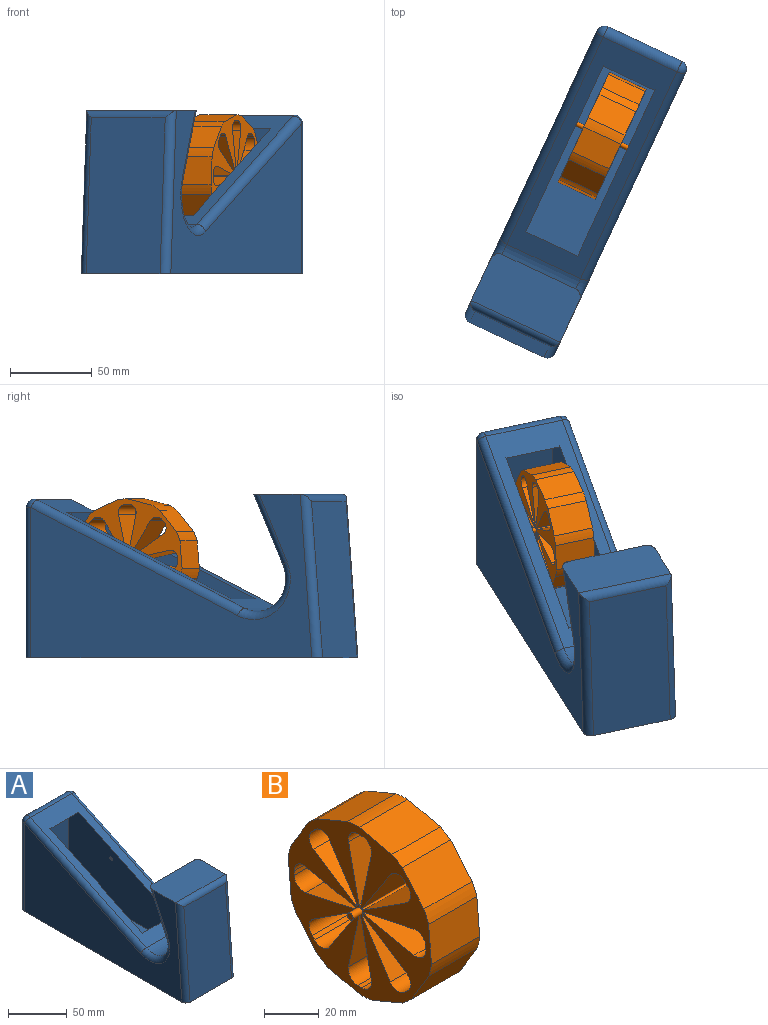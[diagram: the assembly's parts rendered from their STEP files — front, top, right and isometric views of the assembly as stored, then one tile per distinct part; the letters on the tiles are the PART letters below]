
ASSEMBLY  parts=2 mates=1
PART A: 33 faces, bbox 60x200x102.5 mm
  f0: plane 139.81x66.38mm, normal (0,-0.43,0.9), area 3401.7mm2, adj f1,f12,f15,f17,f23,f26,f27,f28
  f1: cylinder r=20mm len=50mm, axis (-1,0,0), area 2441.2mm2, adj f0,f2,f10,f18
  f2: plane 50x43.42mm, normal (0,0.91,-0.41), area 2385.1mm2, adj f1,f3,f9,f19
  f3: plane 60x33.55mm, normal (0,0,1), area 2001.4mm2, adj f2,f7,f8,f9,f19,f20,f21,f22
  f4: plane 95.39x50mm, normal (0,-1,0.08), area 4784.2mm2, adj f5,f20,f21,f22
  f5: plane 200x60mm, normal (0,0,-1), area 11978.5mm2, adj f4,f6,f7,f8,f11,f14,f20,f21
  f6: plane 92.09x50mm, normal (0,1,0), area 4604.6mm2, adj f5,f11,f14,f15
  f7: plane 189.98x100mm, normal (1,0,0), area 10752.2mm2, adj f3,f5,f9,f10,f11,f12,f20
  f8: plane 189.98x100mm, normal (-1,0,0), area 10752.2mm2, adj f3,f5,f14,f17,f18,f19,f21
  f9: cylinder r=5mm len=45.49mm, axis (0,-0.41,-0.91), area 368.2mm2, adj f2,f3,f7,f10
  f10: torus R=25mm, axis (1,0,0), area 418.3mm2, adj f1,f7,f9,f12
  f11: cylinder r=5mm len=92.09mm, axis (0,0,-1), area 723.3mm2, adj f5,f6,f7,f13
  f12: cylinder r=5mm len=141.95mm, axis (0,0.9,0.43), area 1215.5mm2, adj f0,f7,f10,f13
  f13: sphere r=5mm, area 50.4mm2, adj f11,f12,f15
  f14: cylinder r=5mm len=92.09mm, axis (0,0,1), area 723.3mm2, adj f5,f6,f8,f16
  f15: cylinder r=5mm len=50mm, axis (1,0,0), area 503.5mm2, adj f0,f6,f13,f16
  f16: sphere r=5mm, area 50.4mm2, adj f14,f15,f17
  f17: cylinder r=5mm len=141.95mm, axis (0,-0.9,-0.43), area 1215.5mm2, adj f0,f8,f16,f18
  f18: torus R=25mm, axis (1,0,0), area 418.3mm2, adj f1,f8,f17,f19
  f19: cylinder r=5mm len=45.49mm, axis (0,0.41,0.91), area 368.2mm2, adj f2,f3,f8,f18
  f20: cylinder r=5mm len=100.78mm, axis (0,0.08,1), area 775.4mm2, adj f3,f4,f5,f7,f22
  f21: cylinder r=5mm len=100.78mm, axis (0,-0.08,-1), area 775.4mm2, adj f3,f4,f5,f8,f22
  f22: cylinder r=5mm len=59.97mm, axis (-1,0,0), area 419.2mm2, adj f3,f4,f20,f21
  f23: plane 35x28.16mm, normal (0,1,0), area 985.6mm2, adj f0,f24,f27,f28
  f24: plane 124.64x35mm, normal (0,0,1), area 4362.4mm2, adj f23,f25,f27,f28
  f25: plane 81.3x35mm, normal (0,-1,0), area 2845.5mm2, adj f24,f26,f27,f28
  f26: plane 35x12.71mm, normal (0,0,-1), area 445mm2, adj f0,f25,f27,f28
  f27: plane 124.64x81.3mm, normal (1,0,0), area 7152.3mm2, adj f0,f23,f24,f25,f26,f31
  f28: plane 124.64x81.3mm, normal (-1,0,0), area 7152.3mm2, adj f0,f23,f24,f25,f26,f30
  f29: plane 3x3mm, normal (-1,0,0), area 7.1mm2, adj f30
  f30: cylinder r=1.5mm len=5mm, axis (-1,0,0), area 47.1mm2, adj f28,f29
  f31: cylinder r=1.5mm len=5mm, axis (-1,0,0), area 47.1mm2, adj f27,f32
  f32: plane 3x3mm, normal (1,0,0), area 7.1mm2, adj f31
PART B: 74 faces, bbox 35x74.2x75 mm
  f0: cylinder r=37.5mm len=25mm, axis (-1,0,0), area 155.1mm2, adj f52,f53,f68,f69
  f1: cylinder r=37.5mm len=25mm, axis (-1,0,0), area 155.1mm2, adj f52,f53,f67,f68
  f2: cylinder r=37.5mm len=25mm, axis (-1,0,0), area 155.1mm2, adj f52,f53,f66,f67
  f3: cylinder r=37.5mm len=25mm, axis (-1,0,0), area 155.1mm2, adj f52,f53,f65,f66
  f4: cylinder r=37.5mm len=25mm, axis (-1,0,0), area 155.1mm2, adj f52,f53,f64,f65
  f5: cylinder r=37.5mm len=25mm, axis (-1,0,0), area 155.1mm2, adj f52,f53,f63,f64
  f6: cylinder r=37.5mm len=25mm, axis (-1,0,0), area 155.1mm2, adj f52,f53,f62,f63
  f7: cylinder r=37.5mm len=25mm, axis (-1,0,0), area 155.1mm2, adj f52,f53,f61,f62
  f8: cylinder r=37.5mm len=25mm, axis (-1,0,0), area 155.1mm2, adj f52,f53,f60,f61
  f9: plane 25x21.89mm, normal (0,0.84,-0.55), area 653mm2, adj f10,f14,f52,f53
  f10: cylinder r=0.5mm len=25mm, axis (-1,0,0), area 34.1mm2, adj f9,f11,f52,f53
  f11: plane 25x21.89mm, normal (0,-0.55,0.84), area 653mm2, adj f10,f12,f52,f53
  f12: cylinder r=5mm len=25mm, axis (-1,0,0), area 222.4mm2, adj f11,f13,f52,f53
  f13: plane 25x1.43mm, normal (0,-0.71,-0.71), area 50.4mm2, adj f12,f14,f52,f53
  f14: cylinder r=5mm len=25mm, axis (-1,0,0), area 222.4mm2, adj f9,f13,f52,f53
  f15: plane 25.55x25mm, normal (0,0.21,-0.98), area 653mm2, adj f16,f20,f52,f53
  f16: cylinder r=0.5mm len=25mm, axis (-1,0,0), area 34.1mm2, adj f15,f17,f52,f53
  f17: plane 25.55x25mm, normal (0,0.21,0.98), area 653mm2, adj f16,f18,f52,f53
  f18: cylinder r=5mm len=25mm, axis (-1,0,0), area 222.4mm2, adj f17,f19,f52,f53
  f19: plane 25x2.02mm, normal (0,-1,0), area 50.4mm2, adj f18,f20,f52,f53
  f20: cylinder r=5mm len=25mm, axis (-1,0,0), area 222.4mm2, adj f15,f19,f52,f53
  f21: plane 25x21.89mm, normal (0,-0.55,-0.84), area 653mm2, adj f22,f26,f52,f53
  f22: cylinder r=0.5mm len=25mm, axis (-1,0,0), area 34.1mm2, adj f21,f23,f52,f53
  f23: plane 25x21.89mm, normal (0,0.84,0.55), area 653mm2, adj f22,f24,f52,f53
  f24: cylinder r=5mm len=25mm, axis (-1,0,0), area 222.4mm2, adj f23,f25,f52,f53
  f25: plane 25x1.43mm, normal (0,-0.71,0.71), area 50.4mm2, adj f24,f26,f52,f53
  f26: cylinder r=5mm len=25mm, axis (-1,0,0), area 222.4mm2, adj f21,f25,f52,f53
  f27: plane 25.55x25mm, normal (0,-0.98,-0.21), area 653mm2, adj f28,f32,f52,f53
  f28: cylinder r=0.5mm len=25mm, axis (-1,0,0), area 34.1mm2, adj f27,f29,f52,f53
  f29: plane 25.55x25mm, normal (0,0.98,-0.21), area 653mm2, adj f28,f30,f52,f53
  f30: cylinder r=5mm len=25mm, axis (-1,0,0), area 222.4mm2, adj f29,f31,f52,f53
  f31: plane 25x2.02mm, normal (0,0,1), area 50.4mm2, adj f30,f32,f52,f53
  f32: cylinder r=5mm len=25mm, axis (-1,0,0), area 222.4mm2, adj f27,f31,f52,f53
  f33: plane 25x21.89mm, normal (0,-0.84,0.55), area 653mm2, adj f34,f38,f52,f53
  f34: cylinder r=0.5mm len=25mm, axis (-1,0,0), area 34.1mm2, adj f33,f35,f52,f53
  f35: plane 25x21.89mm, normal (0,0.55,-0.84), area 653mm2, adj f34,f36,f52,f53
  f36: cylinder r=5mm len=25mm, axis (-1,0,0), area 222.4mm2, adj f35,f37,f52,f53
  f37: plane 25x1.43mm, normal (0,0.71,0.71), area 50.4mm2, adj f36,f38,f52,f53
  f38: cylinder r=5mm len=25mm, axis (-1,0,0), area 222.4mm2, adj f33,f37,f52,f53
  f39: plane 25.55x25mm, normal (0,-0.21,0.98), area 653mm2, adj f40,f44,f52,f53
  f40: cylinder r=0.5mm len=25mm, axis (-1,0,0), area 34.1mm2, adj f39,f41,f52,f53
  f41: plane 25.55x25mm, normal (0,-0.21,-0.98), area 653mm2, adj f40,f42,f52,f53
  f42: cylinder r=5mm len=25mm, axis (-1,0,0), area 222.4mm2, adj f41,f43,f52,f53
  f43: plane 25x2.02mm, normal (0,1,0), area 50.4mm2, adj f42,f44,f52,f53
  f44: cylinder r=5mm len=25mm, axis (-1,0,0), area 222.4mm2, adj f39,f43,f52,f53
  f45: plane 25x21.89mm, normal (0,0.55,0.84), area 653mm2, adj f46,f50,f52,f53
  f46: cylinder r=0.5mm len=25mm, axis (-1,0,0), area 34.1mm2, adj f45,f47,f52,f53
  f47: plane 25x21.89mm, normal (0,-0.84,-0.55), area 653mm2, adj f46,f48,f52,f53
  f48: cylinder r=5mm len=25mm, axis (-1,0,0), area 222.4mm2, adj f47,f49,f52,f53
  f49: plane 25x1.43mm, normal (0,0.71,-0.71), area 50.4mm2, adj f48,f50,f52,f53
  f50: cylinder r=5mm len=25mm, axis (-1,0,0), area 222.4mm2, adj f45,f49,f52,f53
  f51: cylinder r=37.5mm len=25mm, axis (-1,0,0), area 155.1mm2, adj f52,f53,f60,f69
  f52: plane 75x74.21mm, normal (1,0,0), area 2493.9mm2, adj f0,f1,f2,f3,f4,f5,f6,f7
  f53: plane 75x74.21mm, normal (-1,0,0), area 2493.9mm2, adj f0,f1,f2,f3,f4,f5,f6,f7
  f54: plane 25.55x25mm, normal (0,0.98,0.21), area 653mm2, adj f52,f53,f55,f59
  f55: cylinder r=0.5mm len=25mm, axis (-1,0,0), area 34.1mm2, adj f52,f53,f54,f56
  f56: plane 25.55x25mm, normal (0,-0.98,0.21), area 653mm2, adj f52,f53,f55,f57
  f57: cylinder r=5mm len=25mm, axis (-1,0,0), area 222.4mm2, adj f52,f53,f56,f58
  f58: plane 25x2.02mm, normal (0,0,-1), area 50.4mm2, adj f52,f53,f57,f59
  f59: cylinder r=5mm len=25mm, axis (-1,0,0), area 222.4mm2, adj f52,f53,f54,f58
  f60: plane 25x14.74mm, normal (0,0.86,0.52), area 430.1mm2, adj f8,f51,f52,f53
  f61: plane 25x17.14mm, normal (0,1,-0.09), area 430.1mm2, adj f7,f8,f52,f53
  f62: plane 25x13mm, normal (0,0.76,-0.66), area 430.1mm2, adj f6,f7,f52,f53
  f63: plane 25x16.76mm, normal (0,0.23,-0.97), area 430.1mm2, adj f5,f6,f52,f53
  f64: plane 25x15.84mm, normal (0,-0.39,-0.92), area 430.1mm2, adj f4,f5,f52,f53
  f65: plane 25x14.74mm, normal (0,-0.86,-0.52), area 430.1mm2, adj f3,f4,f52,f53
  f66: plane 25x17.14mm, normal (0,-1,0.09), area 430.1mm2, adj f2,f3,f52,f53
  f67: plane 25x13mm, normal (0,-0.76,0.66), area 430.1mm2, adj f1,f2,f52,f53
  f68: plane 25x16.76mm, normal (0,-0.23,0.97), area 430.1mm2, adj f0,f1,f52,f53
  f69: plane 25x15.84mm, normal (0,0.39,0.92), area 430.1mm2, adj f0,f51,f52,f53
  f70: plane 3x3mm, normal (-1,0,0), area 7.1mm2, adj f71
  f71: cylinder r=1.5mm len=5mm, axis (-1,0,0), area 47.1mm2, adj f53,f70
  f72: cylinder r=1.5mm len=5mm, axis (-1,0,0), area 47.1mm2, adj f52,f73
  f73: plane 3x3mm, normal (1,0,0), area 7.1mm2, adj f72
PLACE A rot(axis=(0,0,-1),25deg) t=(-40.18,-42.8,-23.95)mm
PLACE B rot(axis=(0,0,-1),25deg) t=(-24.14,-8.39,-11.49)mm
MATE revolute B.f0 <-> A.f30  axis (0.91,-0.42,0) through (-8.28,-15.79,-11.49)mm
